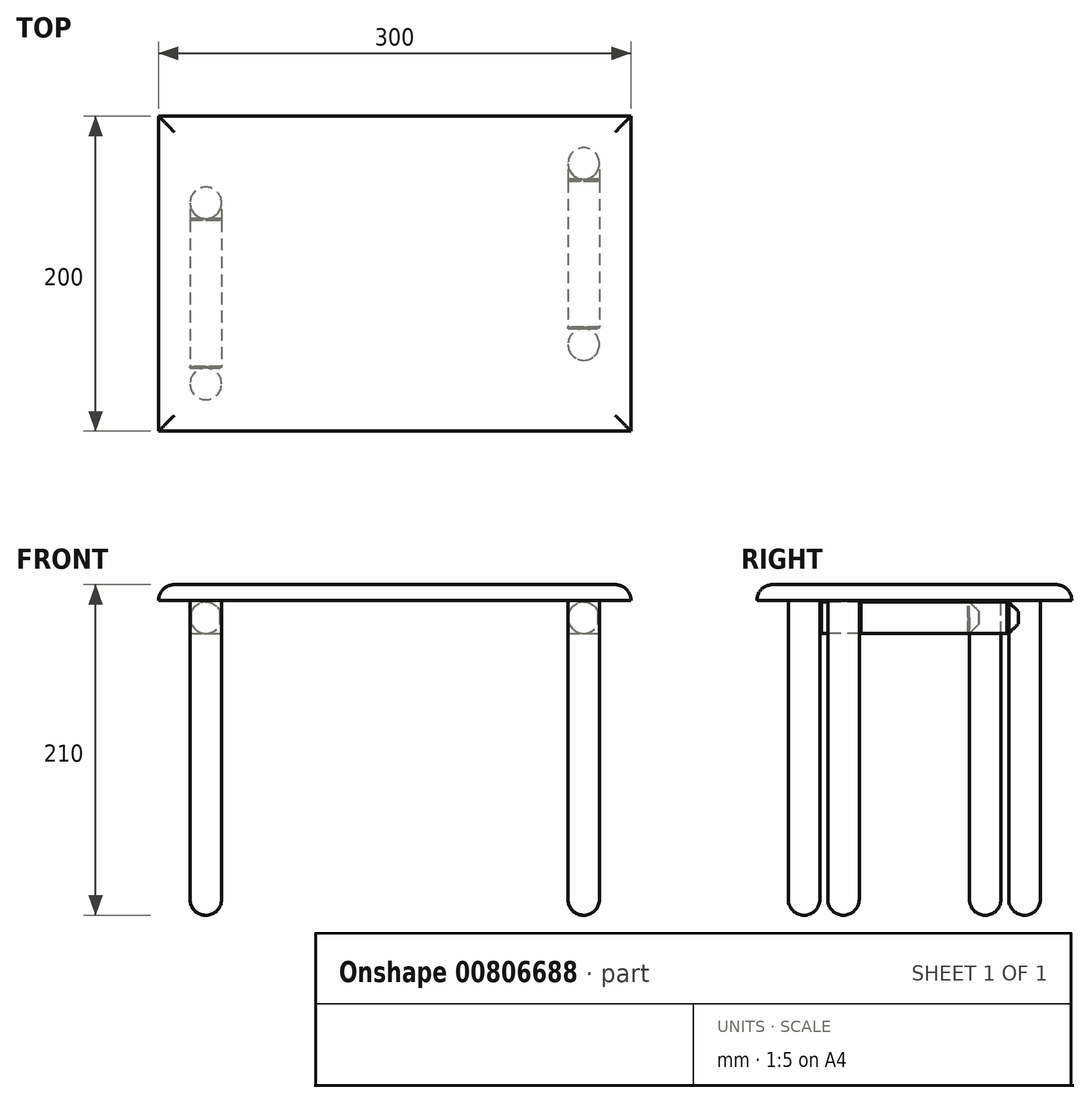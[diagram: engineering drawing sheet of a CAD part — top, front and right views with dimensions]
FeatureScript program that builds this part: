
annotation { "Feature Type Name" : "Feature", "Feature Type Description" : "" }
export const myFeature = defineFeature(function(context is Context, id is Id, definition is map)
    precondition{}
    {
        {
            var Q0;
            Q0=qCreatedBy(makeId("Top.planeOp"),FACE);
            var sketch = newSketch(context, id + "F0", { "sketchPlane" : qUnion([Q0])});
            skLineSegment(sketch, "E0.bottom", {"start": v(-155.76, 99.86) * mm, "end": v(144.24, 99.86) * mm});
            skLineSegment(sketch, "E0.top", {"start": v(-155.76, -100.14) * mm, "end": v(144.24, -100.14) * mm});
            skLineSegment(sketch, "E0.left", {"start": v(-155.76, 99.86) * mm, "end": v(-155.76, -100.14) * mm});
            skLineSegment(sketch, "E0.right", {"start": v(144.24, 99.86) * mm, "end": v(144.24, -100.14) * mm});
            skSolve(sketch);
        }
        {
            var Q0;
            Q0=makeQuery(id+"F0.imprint","IMPRINT",FACE,{"disambiguationData":[TD([[makeQuery(id+"F0.imprint","IMPRINT",EDGE,{"derivedFrom":sQuery(id+"F0.wireOp",EDGE,"E0.bottom")}),-1.0]])]});
            extrude(context, id + "F1", {"entities" : qUnion([Q0]), "depth" : 10 * mm, "offsetDistance" : 25.4 * mm});
        }
        {
            var Q0;
            Q0=makeQuery(id+"F1.opExtrude","CAP_FACE",FACE,{"disambiguationData":[OSD([sQuery(id+"F0.wireOp",EDGE,"E0.bottom"),sQuery(id+"F0.wireOp",EDGE,"E0.top"),sQuery(id+"F0.wireOp",EDGE,"E0.left"),sQuery(id+"F0.wireOp",EDGE,"E0.right")])],"isStart":true});
            var sketch = newSketch(context, id + "F2", { "sketchPlane" : qUnion([Q0])});
            skCircle(sketch, "E1", {"center": v(-125.76, 70.14) * mm, "radius": 10 * mm});
            skCircle(sketch, "E2", {"center": v(114.24, -69.86) * mm, "radius": 10 * mm});
            skCircle(sketch, "E3", {"center": v(-125.76, -44.86) * mm, "radius": 10 * mm});
            skCircle(sketch, "E4", {"center": v(114.24, 45.14) * mm, "radius": 10 * mm});
            skSolve(sketch);
        }
        {
            var Q0;
            Q0=makeQuery(id+"F2.imprint","IMPRINT",FACE,{"disambiguationData":[TD([[makeQuery(id+"F2.imprint","IMPRINT",EDGE,{"derivedFrom":sQuery(id+"F2.wireOp",EDGE,"E1")}),1.0]])]});
            var Q1;
            Q1=makeQuery(id+"F2.imprint","IMPRINT",FACE,{"disambiguationData":[TD([[makeQuery(id+"F2.imprint","IMPRINT",EDGE,{"derivedFrom":sQuery(id+"F2.wireOp",EDGE,"E3")}),1.0]])]});
            var Q2;
            Q2=makeQuery(id+"F2.imprint","IMPRINT",FACE,{"disambiguationData":[TD([[makeQuery(id+"F2.imprint","IMPRINT",EDGE,{"derivedFrom":sQuery(id+"F2.wireOp",EDGE,"E4")}),1.0]])]});
            var Q3;
            Q3=makeQuery(id+"F2.imprint","IMPRINT",FACE,{"disambiguationData":[TD([[makeQuery(id+"F2.imprint","IMPRINT",EDGE,{"derivedFrom":sQuery(id+"F2.wireOp",EDGE,"E2")}),1.0]])]});
            extrude(context, id + "F3", {"entities" : qUnion([Q0, Q1, Q2, Q3]), "operationType" : NewBodyOperationType.ADD, "depth" : 200 * mm, "offsetDistance" : 25.4 * mm});
        }
        {
            var Q0;
            Q0=makeQuery(id+"F3.opExtrude","CAP_EDGE",EDGE,{"disambiguationData":[OSD([sQuery(id+"F2.wireOp",EDGE,"E1")])],"isStart":false});
            var Q1;
            Q1=makeQuery(id+"F3.opExtrude","CAP_EDGE",EDGE,{"disambiguationData":[OSD([sQuery(id+"F2.wireOp",EDGE,"E3")])],"isStart":false});
            var Q2;
            Q2=makeQuery(id+"F3.opExtrude","CAP_FACE",FACE,{"disambiguationData":[OSD([sQuery(id+"F2.wireOp",EDGE,"E4")])],"isStart":false});
            var Q3;
            Q3=makeQuery(id+"F3.opExtrude","CAP_EDGE",EDGE,{"disambiguationData":[OSD([sQuery(id+"F2.wireOp",EDGE,"E2")])],"isStart":false});
            fillet(context, id + "F4", {"entities" : qUnion([Q0, Q1, Q2, Q3]), "radius" : 10 * mm, "tangentPropagation" : true, "allowEdgeOverflow" : false});
        }
        {
            var Q0;
            Q0=makeQuery(id+"F1.opExtrude","CAP_FACE",FACE,{"disambiguationData":[OSD([sQuery(id+"F0.wireOp",EDGE,"E0.bottom"),sQuery(id+"F0.wireOp",EDGE,"E0.top"),sQuery(id+"F0.wireOp",EDGE,"E0.left"),sQuery(id+"F0.wireOp",EDGE,"E0.right")])],"isStart":true});
            var sketch = newSketch(context, id + "F5", { "sketchPlane" : qUnion([Q0])});
            skLineSegment(sketch, "E5.bottom", {"start": v(-135.76, 60.1) * mm, "end": v(-115.76, 60.1) * mm});
            skLineSegment(sketch, "E5.top", {"start": v(-135.76, 59.1) * mm, "end": v(-115.76, 59.1) * mm});
            skLineSegment(sketch, "E5.left", {"start": v(-135.76, 60.1) * mm, "end": v(-135.76, 59.1) * mm});
            skLineSegment(sketch, "E5.right", {"start": v(-115.76, 60.1) * mm, "end": v(-115.76, 59.1) * mm});
            skLineSegment(sketch, "E6.bottom", {"start": v(-135.76, -34.8) * mm, "end": v(-115.76, -34.8) * mm});
            skLineSegment(sketch, "E6.top", {"start": v(-135.76, -33.8) * mm, "end": v(-115.76, -33.8) * mm});
            skLineSegment(sketch, "E6.left", {"start": v(-135.76, -34.8) * mm, "end": v(-135.76, -33.8) * mm});
            skLineSegment(sketch, "E6.right", {"start": v(-115.76, -34.8) * mm, "end": v(-115.76, -33.8) * mm});
            skLineSegment(sketch, "E7.bottom", {"start": v(104.24, -59.8) * mm, "end": v(124.24, -59.8) * mm});
            skLineSegment(sketch, "E7.top", {"start": v(104.24, -58.8) * mm, "end": v(124.24, -58.8) * mm});
            skLineSegment(sketch, "E7.left", {"start": v(104.24, -59.8) * mm, "end": v(104.24, -58.8) * mm});
            skLineSegment(sketch, "E7.right", {"start": v(124.24, -59.8) * mm, "end": v(124.24, -58.8) * mm});
            skLineSegment(sketch, "E8.bottom", {"start": v(104.24, 35.1) * mm, "end": v(124.24, 35.1) * mm});
            skLineSegment(sketch, "E8.top", {"start": v(104.24, 34.1) * mm, "end": v(124.24, 34.1) * mm});
            skLineSegment(sketch, "E8.left", {"start": v(104.24, 35.1) * mm, "end": v(104.24, 34.1) * mm});
            skLineSegment(sketch, "E8.right", {"start": v(124.24, 35.1) * mm, "end": v(124.24, 34.1) * mm});
            skSolve(sketch);
        }
        {
            var Q0;
            Q0=makeQuery(id+"F5.imprint","IMPRINT",FACE,{"disambiguationData":[TD([[makeQuery(id+"F5.imprint","IMPRINT",EDGE,{"derivedFrom":sQuery(id+"F5.wireOp",EDGE,"E5.top")}),1.0]])]});
            var Q1;
            Q1=makeQuery(id+"F5.imprint","IMPRINT",FACE,{"disambiguationData":[TD([[makeQuery(id+"F5.imprint","IMPRINT",EDGE,{"derivedFrom":sQuery(id+"F5.wireOp",EDGE,"E6.top")}),-1.0]])]});
            var Q2;
            Q2=makeQuery(id+"F5.imprint","IMPRINT",FACE,{"disambiguationData":[TD([[makeQuery(id+"F5.imprint","IMPRINT",EDGE,{"derivedFrom":sQuery(id+"F5.wireOp",EDGE,"E7.top")}),-1.0]])]});
            var Q3;
            Q3=makeQuery(id+"F5.imprint","IMPRINT",FACE,{"disambiguationData":[TD([[makeQuery(id+"F5.imprint","IMPRINT",EDGE,{"derivedFrom":sQuery(id+"F5.wireOp",EDGE,"E8.top")}),1.0]])]});
            extrude(context, id + "F6", {"entities" : qUnion([Q0, Q1, Q2, Q3]), "operationType" : NewBodyOperationType.ADD, "depth" : 21 * mm, "offsetDistance" : 25.4 * mm});
        }
        {
            var Q0;
            Q0=makeQuery(id+"F6.opExtrude","SWEPT_FACE",FACE,{"disambiguationData":[OSD([sQuery(id+"F5.wireOp",EDGE,"E5.top")])]});
            var sketch = newSketch(context, id + "F7", { "sketchPlane" : qUnion([Q0])});
            skCircle(sketch, "E9", {"center": v(125.76, -11) * mm, "radius": 10 * mm});
            skSolve(sketch);
        }
        {
            var Q0;
            Q0=makeQuery(id+"F6.opExtrude","SWEPT_FACE",FACE,{"disambiguationData":[OSD([sQuery(id+"F5.wireOp",EDGE,"E8.top")])]});
            var sketch = newSketch(context, id + "F8", { "sketchPlane" : qUnion([Q0])});
            skCircle(sketch, "E10", {"center": v(-114.24, -11) * mm, "radius": 10 * mm});
            skSolve(sketch);
        }
        {
            var Q0;
            {var subQ0=sQuery(id+"F7.wireOp",EDGE,"E9");var subQ1=sQuery(id+"F5.wireOp",EDGE,"E5.top");var subQ4=makeQuery(id+"F7.imprint","INTERSECT",VERTEX,{"derivedFrom":[makeQuery(id+"F6.opExtrude","CAP_EDGE",EDGE,{"disambiguationData":[OSD([subQ1])],"isStart":false}),subQ0]});Q0=makeQuery(id+"F7.imprint","IMPRINT",FACE,{"disambiguationData":[TD([[makeQuery(id+"F7.imprint","IMPRINT",EDGE,{"disambiguationData":[TD([[subQ4,1.0]])],"derivedFrom":subQ0}),1.0]])]});}
            var Q1;
            {var subQ0=sQuery(id+"F8.wireOp",EDGE,"E10");var subQ1=sQuery(id+"F5.wireOp",EDGE,"E8.top");var subQ4=makeQuery(id+"F8.imprint","INTERSECT",VERTEX,{"derivedFrom":[makeQuery(id+"F6.opExtrude","CAP_EDGE",EDGE,{"disambiguationData":[OSD([subQ1])],"isStart":false}),subQ0]});Q1=makeQuery(id+"F8.imprint","IMPRINT",FACE,{"disambiguationData":[TD([[makeQuery(id+"F8.imprint","IMPRINT",EDGE,{"disambiguationData":[TD([[subQ4,1.0]])],"derivedFrom":subQ0}),1.0]])]});}
            extrude(context, id + "F9", {"entities" : qUnion([Q0, Q1]), "operationType" : NewBodyOperationType.ADD, "depth" : 100 * mm, "offsetDistance" : 25.4 * mm});
        }
        {
            var Q0;
            Q0=makeQuery(id+"F1.opExtrude","CAP_EDGE",EDGE,{"disambiguationData":[OSD([sQuery(id+"F0.wireOp",EDGE,"E0.left")])],"isStart":false});
            var Q1;
            Q1=makeQuery(id+"F1.opExtrude","CAP_EDGE",EDGE,{"disambiguationData":[OSD([sQuery(id+"F0.wireOp",EDGE,"E0.bottom")])],"isStart":false});
            var Q2;
            Q2=makeQuery(id+"F1.opExtrude","CAP_EDGE",EDGE,{"disambiguationData":[OSD([sQuery(id+"F0.wireOp",EDGE,"E0.right")])],"isStart":false});
            var Q3;
            Q3=makeQuery(id+"F1.opExtrude","CAP_EDGE",EDGE,{"disambiguationData":[OSD([sQuery(id+"F0.wireOp",EDGE,"E0.top")])],"isStart":false});
            fillet(context, id + "F10", {"entities" : qUnion([Q0, Q1, Q2, Q3]), "radius" : 10 * mm, "tangentPropagation" : true, "allowEdgeOverflow" : false});
        }
    });
